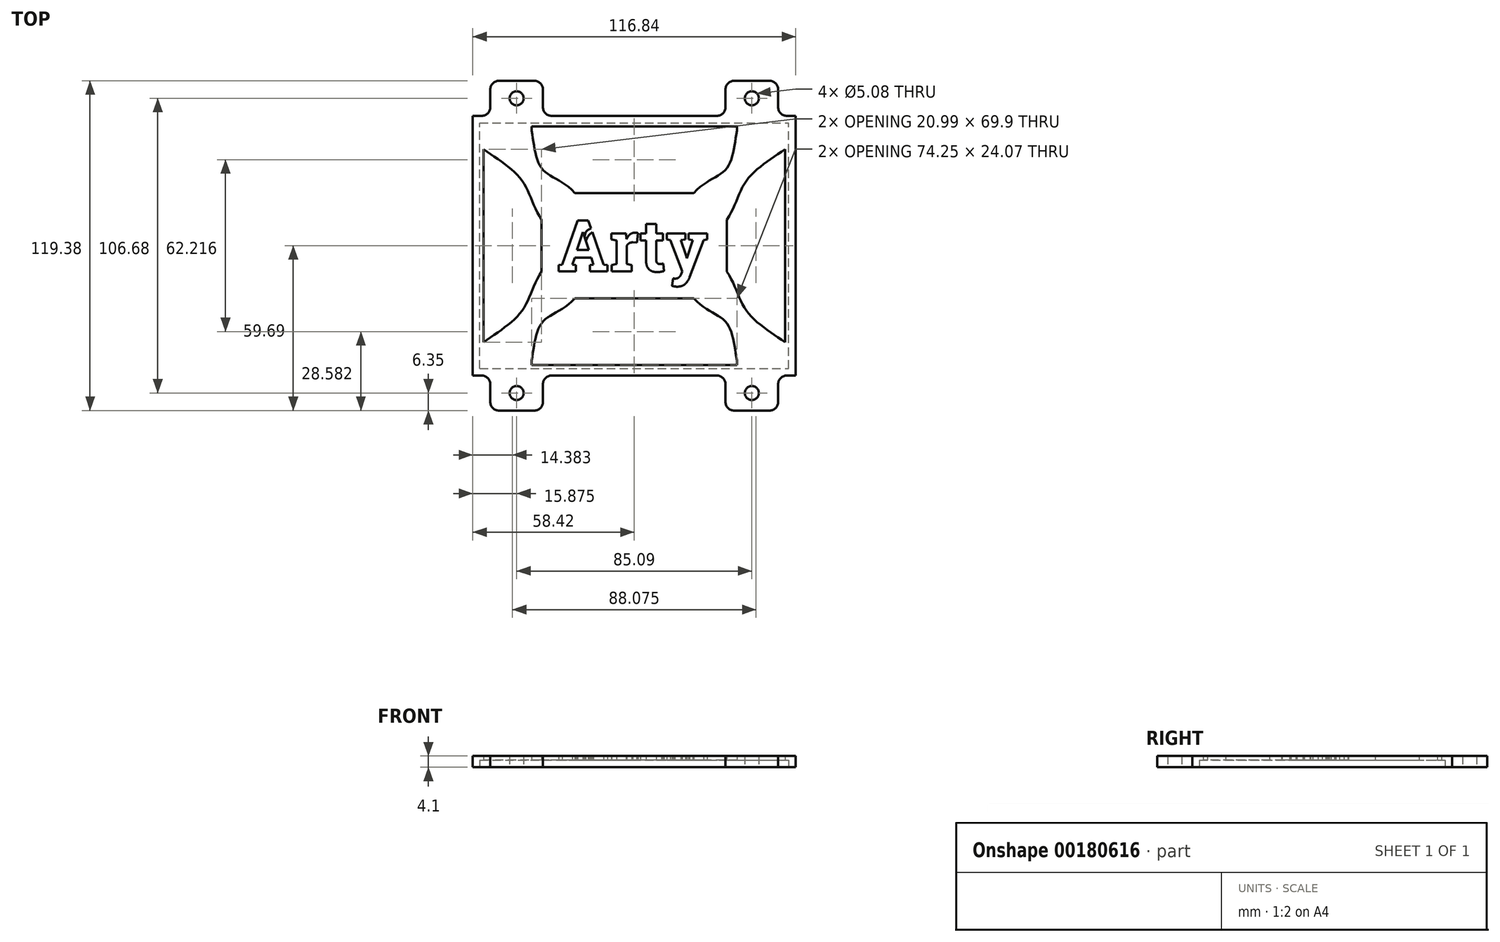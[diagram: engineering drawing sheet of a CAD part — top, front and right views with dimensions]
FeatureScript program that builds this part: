
annotation { "Feature Type Name" : "Feature", "Feature Type Description" : "" }
export const myFeature = defineFeature(function(context is Context, id is Id, definition is map)
    precondition{}
    {
        {
            var Q0;
            Q0=qCreatedBy(makeId("Top.planeOp"),FACE);
            var sketch = newSketch(context, id + "F0", { "sketchPlane" : qUnion([Q0])});
            skLineSegment(sketch, "E0.bottom", {"start": v(58.42, -46.99) * mm, "end": v(-58.42, -46.99) * mm});
            skLineSegment(sketch, "E0.top", {"start": v(58.42, 47) * mm, "end": v(-58.42, 46.99) * mm});
            skLineSegment(sketch, "E0.left", {"start": v(58.42, -46.99) * mm, "end": v(58.42, 47) * mm});
            skLineSegment(sketch, "E0.right", {"start": v(-58.42, -46.99) * mm, "end": v(-58.42, 46.99) * mm});
            skPoint(sketch, "E1", {"position": v(-58.42, 0) * mm});
            skPoint(sketch, "E2", {"position": v(0, 47) * mm});
            skSolve(sketch);
        }
        {
            var Q0;
            Q0 = qSketchRegion(id + "F0", true);
            extrude(context, id + "F1", {"entities" : qUnion([Q0]), "depth" : 4.1 * mm});
        }
        {
            var Q0;
            Q0=qCreatedBy(makeId("Top.planeOp"),FACE);
            var sketch = newSketch(context, id + "F2", { "sketchPlane" : qUnion([Q0])});
            skLineSegment(sketch, "E3.bottom", {"start": v(-55.88, -44.45) * mm, "end": v(55.88, -44.45) * mm});
            skLineSegment(sketch, "E3.top", {"start": v(-55.88, 44.45) * mm, "end": v(55.88, 44.45) * mm});
            skLineSegment(sketch, "E3.left", {"start": v(-55.88, -44.45) * mm, "end": v(-55.88, 44.45) * mm});
            skLineSegment(sketch, "E3.right", {"start": v(55.88, -44.45) * mm, "end": v(55.88, 44.45) * mm});
            skPoint(sketch, "E4", {"position": v(0, 44.45) * mm});
            skPoint(sketch, "E5", {"position": v(55.88, 0) * mm});
            skSolve(sketch);
        }
        {
            var Q0;
            Q0=makeQuery(id+"F2.imprint","IMPRINT",FACE,{"disambiguationData":[TD([[makeQuery(id+"F2.imprint","IMPRINT",EDGE,{"derivedFrom":sQuery(id+"F2.wireOp",EDGE,"E3.bottom")}),1.0]])]});
            extrude(context, id + "F3", {"entities" : qUnion([Q0]), "operationType" : NewBodyOperationType.REMOVE, "depth" : 2.54 * mm});
        }
        {
            var Q0;
            Q0=makeQuery(id+"F1.opExtrude","SWEPT_FACE",FACE,{"disambiguationData":[OSD([sQuery(id+"F0.wireOp",EDGE,"E0.top")])]});
            var sketch = newSketch(context, id + "F4", { "sketchPlane" : qUnion([Q0])});
            skLineSegment(sketch, "E6.bottom", {"start": v(52.07, 0) * mm, "end": v(33.02, 0) * mm});
            skLineSegment(sketch, "E6.top", {"start": v(52.07, 4.1) * mm, "end": v(33.02, 4.1) * mm});
            skLineSegment(sketch, "E6.left", {"start": v(52.07, 0) * mm, "end": v(52.07, 4.1) * mm});
            skLineSegment(sketch, "E6.right", {"start": v(33.02, 0) * mm, "end": v(33.02, 4.1) * mm});
            skPoint(sketch, "E7", {"position": v(58.42, 0) * mm});
            skPoint(sketch, "E8.MirrorP", {"position": v(-58.42, 0) * mm});
            skLineSegment(sketch, "E9.MirrorCS", {"start": v(-52.07, 0) * mm, "end": v(-52.07, 4.1) * mm});
            skLineSegment(sketch, "E10.MirrorCS", {"start": v(-52.07, 0) * mm, "end": v(-33.02, 0) * mm});
            skLineSegment(sketch, "E11.MirrorCS", {"start": v(-33.02, 0) * mm, "end": v(-33.02, 4.1) * mm});
            skLineSegment(sketch, "E12.MirrorCS", {"start": v(-52.07, 4.1) * mm, "end": v(-33.02, 4.1) * mm});
            skSolve(sketch);
        }
        {
            var Q0;
            Q0 = qSketchRegion(id + "F4", true);
            extrude(context, id + "F5", {"entities" : qUnion([Q0]), "operationType" : NewBodyOperationType.ADD, "depth" : 12.7 * mm});
        }
        {
            var Q0;
            Q0=makeQuery(id+"F1.opExtrude","SWEPT_FACE",FACE,{"disambiguationData":[OSD([sQuery(id+"F0.wireOp",EDGE,"E0.bottom")])]});
            var sketch = newSketch(context, id + "F6", { "sketchPlane" : qUnion([Q0])});
            skLineSegment(sketch, "E13.bottom", {"start": v(-52.07, 4.1) * mm, "end": v(-33.02, 4.1) * mm});
            skLineSegment(sketch, "E13.top", {"start": v(-52.07, 0) * mm, "end": v(-33.02, 0) * mm});
            skLineSegment(sketch, "E13.left", {"start": v(-52.07, 4.1) * mm, "end": v(-52.07, 0) * mm});
            skLineSegment(sketch, "E13.right", {"start": v(-33.02, 4.1) * mm, "end": v(-33.02, 0) * mm});
            skPoint(sketch, "E14", {"position": v(-58.42, 0) * mm});
            skLineSegment(sketch, "E15.MirrorCS", {"start": v(52.07, 0) * mm, "end": v(33.02, 0) * mm});
            skLineSegment(sketch, "E16.MirrorCS", {"start": v(33.02, 4.1) * mm, "end": v(33.02, 0) * mm});
            skLineSegment(sketch, "E17.MirrorCS", {"start": v(52.07, 4.1) * mm, "end": v(33.02, 4.1) * mm});
            skLineSegment(sketch, "E18.MirrorCS", {"start": v(52.07, 4.1) * mm, "end": v(52.07, 0) * mm});
            skPoint(sketch, "E19.MirrorP", {"position": v(58.42, 0) * mm});
            skSolve(sketch);
        }
        {
            var Q0;
            Q0 = qSketchRegion(id + "F6", true);
            extrude(context, id + "F7", {"entities" : qUnion([Q0]), "operationType" : NewBodyOperationType.ADD, "depth" : 12.7 * mm});
        }
        {
            var Q0;
            Q0=makeQuery(id+"F7.boolean.opBoolean","MERGE",FACE,{"derivedFrom":[makeQuery(id+"F5.boolean.opBoolean","MERGE",FACE,{"derivedFrom":[makeQuery(id+"F1.opExtrude","CAP_FACE",FACE,{"disambiguationData":[OSD([sQuery(id+"F0.wireOp",EDGE,"E0.bottom"),sQuery(id+"F0.wireOp",EDGE,"E0.top"),sQuery(id+"F0.wireOp",EDGE,"E0.left"),sQuery(id+"F0.wireOp",EDGE,"E0.right")])],"isStart":true}),makeQuery(id+"F5.opExtrude","SWEPT_FACE",FACE,{"disambiguationData":[OSD([sQuery(id+"F4.wireOp",EDGE,"E6.bottom")])]}),makeQuery(id+"F5.opExtrude","SWEPT_FACE",FACE,{"disambiguationData":[OSD([sQuery(id+"F4.wireOp",EDGE,"E10.MirrorCS")])]})]}),makeQuery(id+"F7.opExtrude","SWEPT_FACE",FACE,{"disambiguationData":[OSD([sQuery(id+"F6.wireOp",EDGE,"E13.top")])]}),makeQuery(id+"F7.opExtrude","SWEPT_FACE",FACE,{"disambiguationData":[OSD([sQuery(id+"F6.wireOp",EDGE,"E15.MirrorCS")])]})]});
            var sketch = newSketch(context, id + "F8", { "sketchPlane" : qUnion([Q0])});
            skPoint(sketch, "E20.visualSharp", {"position": v(52.07, 59.69) * mm});
            skArc(sketch, "E20.filletArc", {"start": v(52.07, 56.51) * mm, "mid": v(51.14, 58.76) * mm, "end": v(48.9, 59.69) * mm});
            skPoint(sketch, "E21.visualSharp", {"position": v(33.02, 59.69) * mm});
            skArc(sketch, "E21.filletArc", {"start": v(36.2, 59.69) * mm, "mid": v(33.95, 58.76) * mm, "end": v(33.02, 56.51) * mm});
            skArc(sketch, "E22.MirrorCS", {"start": v(-36.2, 59.69) * mm, "mid": v(-33.95, 58.76) * mm, "end": v(-33.02, 56.51) * mm});
            skPoint(sketch, "E23.MirrorP", {"position": v(-52.07, 59.69) * mm});
            skArc(sketch, "E24.MirrorCS", {"start": v(-52.07, 56.51) * mm, "mid": v(-51.14, 58.76) * mm, "end": v(-48.9, 59.69) * mm});
            skArc(sketch, "E25.MirrorCS", {"start": v(-52.07, -56.51) * mm, "mid": v(-51.14, -58.76) * mm, "end": v(-48.9, -59.69) * mm});
            skArc(sketch, "E26.MirrorCS", {"start": v(-36.2, -59.69) * mm, "mid": v(-33.95, -58.76) * mm, "end": v(-33.02, -56.51) * mm});
            skArc(sketch, "E27.MirrorCS", {"start": v(36.2, -59.69) * mm, "mid": v(33.95, -58.76) * mm, "end": v(33.02, -56.51) * mm});
            skArc(sketch, "E28.MirrorCS", {"start": v(52.07, -56.51) * mm, "mid": v(51.14, -58.76) * mm, "end": v(48.9, -59.69) * mm});
            skLineSegment(sketch, "E29", {"start": v(33.02, 59.69) * mm, "end": v(33.02, 56.51) * mm});
            skLineSegment(sketch, "E30", {"start": v(33.02, 59.69) * mm, "end": v(36.2, 59.69) * mm});
            skLineSegment(sketch, "E31", {"start": v(48.9, 59.69) * mm, "end": v(52.07, 59.69) * mm});
            skLineSegment(sketch, "E32", {"start": v(52.07, 56.51) * mm, "end": v(52.07, 59.69) * mm});
            skLineSegment(sketch, "E33.MirrorCS", {"start": v(-33.02, 59.69) * mm, "end": v(-33.02, 56.51) * mm});
            skLineSegment(sketch, "E34.MirrorCS", {"start": v(-33.02, 59.69) * mm, "end": v(-36.2, 59.69) * mm});
            skLineSegment(sketch, "E35.MirrorCS", {"start": v(-48.9, 59.69) * mm, "end": v(-52.07, 59.69) * mm});
            skLineSegment(sketch, "E36.MirrorCS", {"start": v(-52.07, 56.51) * mm, "end": v(-52.07, 59.69) * mm});
            skLineSegment(sketch, "E37.MirrorCS", {"start": v(-52.07, -56.51) * mm, "end": v(-52.07, -59.69) * mm});
            skLineSegment(sketch, "E38.MirrorCS", {"start": v(-48.9, -59.69) * mm, "end": v(-52.07, -59.69) * mm});
            skLineSegment(sketch, "E39.MirrorCS", {"start": v(-33.02, -59.69) * mm, "end": v(-36.2, -59.69) * mm});
            skLineSegment(sketch, "E40.MirrorCS", {"start": v(-33.02, -59.69) * mm, "end": v(-33.02, -56.51) * mm});
            skLineSegment(sketch, "E41.MirrorCS", {"start": v(52.07, -56.51) * mm, "end": v(52.07, -59.69) * mm});
            skLineSegment(sketch, "E42.MirrorCS", {"start": v(48.9, -59.69) * mm, "end": v(52.07, -59.69) * mm});
            skLineSegment(sketch, "E43.MirrorCS", {"start": v(33.02, -59.69) * mm, "end": v(33.02, -56.51) * mm});
            skLineSegment(sketch, "E44.MirrorCS", {"start": v(33.02, -59.69) * mm, "end": v(36.2, -59.69) * mm});
            skSolve(sketch);
        }
        {
            var Q0;
            Q0 = qSketchRegion(id + "F8", true);
            extrude(context, id + "F9", {"entities" : qUnion([Q0]), "operationType" : NewBodyOperationType.REMOVE, "oppositeDirection" : true, "depth" : 4.1 * mm});
        }
        {
            var Q0;
            Q0=makeQuery(id+"F7.boolean.opBoolean","MERGE",FACE,{"derivedFrom":[makeQuery(id+"F5.boolean.opBoolean","MERGE",FACE,{"derivedFrom":[makeQuery(id+"F1.opExtrude","CAP_FACE",FACE,{"disambiguationData":[OSD([sQuery(id+"F0.wireOp",EDGE,"E0.bottom"),sQuery(id+"F0.wireOp",EDGE,"E0.top"),sQuery(id+"F0.wireOp",EDGE,"E0.left"),sQuery(id+"F0.wireOp",EDGE,"E0.right")])],"isStart":true}),makeQuery(id+"F5.opExtrude","SWEPT_FACE",FACE,{"disambiguationData":[OSD([sQuery(id+"F4.wireOp",EDGE,"E6.bottom")])]}),makeQuery(id+"F5.opExtrude","SWEPT_FACE",FACE,{"disambiguationData":[OSD([sQuery(id+"F4.wireOp",EDGE,"E10.MirrorCS")])]})]}),makeQuery(id+"F7.opExtrude","SWEPT_FACE",FACE,{"disambiguationData":[OSD([sQuery(id+"F6.wireOp",EDGE,"E13.top")])]}),makeQuery(id+"F7.opExtrude","SWEPT_FACE",FACE,{"disambiguationData":[OSD([sQuery(id+"F6.wireOp",EDGE,"E15.MirrorCS")])]})]});
            var sketch = newSketch(context, id + "F10", { "sketchPlane" : qUnion([Q0])});
            skPoint(sketch, "E45.visualSharp", {"position": v(-52.07, -46.99) * mm});
            skArc(sketch, "E45.filletArc", {"start": v(-52.07, -50.16) * mm, "mid": v(-53, -47.92) * mm, "end": v(-55.25, -46.99) * mm});
            skPoint(sketch, "E46.visualSharp", {"position": v(-33.02, -46.99) * mm});
            skArc(sketch, "E46.filletArc", {"start": v(-29.84, -46.99) * mm, "mid": v(-32.1, -47.92) * mm, "end": v(-33.02, -50.16) * mm});
            skLineSegment(sketch, "E47", {"start": v(-52.07, -46.99) * mm, "end": v(-52.07, -50.16) * mm});
            skLineSegment(sketch, "E48", {"start": v(-55.25, -46.99) * mm, "end": v(-52.07, -46.99) * mm});
            skLineSegment(sketch, "E49", {"start": v(-33.02, -50.16) * mm, "end": v(-33.02, -46.99) * mm});
            skLineSegment(sketch, "E50.MirrorCS", {"start": v(55.25, -46.99) * mm, "end": v(52.07, -46.99) * mm});
            skLineSegment(sketch, "E51.MirrorCS", {"start": v(33.02, -50.16) * mm, "end": v(33.02, -46.99) * mm});
            skArc(sketch, "E52.MirrorCS", {"start": v(29.84, -46.99) * mm, "mid": v(32.1, -47.92) * mm, "end": v(33.02, -50.16) * mm});
            skArc(sketch, "E53.MirrorCS", {"start": v(52.07, -50.16) * mm, "mid": v(53, -47.92) * mm, "end": v(55.25, -46.99) * mm});
            skLineSegment(sketch, "E54.MirrorCS", {"start": v(52.07, -46.99) * mm, "end": v(52.07, -50.16) * mm});
            skPoint(sketch, "E55.MirrorP", {"position": v(52.07, -46.99) * mm});
            skPoint(sketch, "E56.MirrorP", {"position": v(33.02, -46.99) * mm});
            skLineSegment(sketch, "E57.MirrorCS", {"start": v(52.07, 46.99) * mm, "end": v(52.07, 50.16) * mm});
            skLineSegment(sketch, "E58.MirrorCS", {"start": v(-55.25, 46.99) * mm, "end": v(-52.07, 46.99) * mm});
            skLineSegment(sketch, "E59.MirrorCS", {"start": v(55.25, 46.99) * mm, "end": v(52.07, 46.99) * mm});
            skArc(sketch, "E60.MirrorCS", {"start": v(52.07, 50.16) * mm, "mid": v(53, 47.92) * mm, "end": v(55.25, 46.99) * mm});
            skLineSegment(sketch, "E61.MirrorCS", {"start": v(-33.02, 50.16) * mm, "end": v(-33.02, 46.99) * mm});
            skLineSegment(sketch, "E62.MirrorCS", {"start": v(-52.07, 46.99) * mm, "end": v(-52.07, 50.16) * mm});
            skArc(sketch, "E63.MirrorCS", {"start": v(-52.07, 50.16) * mm, "mid": v(-53, 47.92) * mm, "end": v(-55.25, 46.99) * mm});
            skArc(sketch, "E64.MirrorCS", {"start": v(-29.84, 46.99) * mm, "mid": v(-32.1, 47.92) * mm, "end": v(-33.02, 50.16) * mm});
            skArc(sketch, "E65.MirrorCS", {"start": v(29.84, 46.99) * mm, "mid": v(32.1, 47.92) * mm, "end": v(33.02, 50.16) * mm});
            skLineSegment(sketch, "E66.MirrorCS", {"start": v(33.02, 50.16) * mm, "end": v(33.02, 46.99) * mm});
            skPoint(sketch, "E67.MirrorP", {"position": v(-52.07, 46.99) * mm});
            skPoint(sketch, "E68.MirrorP", {"position": v(-33.02, 46.99) * mm});
            skPoint(sketch, "E69.MirrorP", {"position": v(33.02, 46.99) * mm});
            skPoint(sketch, "E70.MirrorP", {"position": v(52.07, 46.99) * mm});
            skLineSegment(sketch, "E71", {"start": v(-33.02, -46.99) * mm, "end": v(-29.84, -46.99) * mm});
            skLineSegment(sketch, "E72", {"start": v(33.02, -46.99) * mm, "end": v(29.84, -46.99) * mm});
            skLineSegment(sketch, "E73", {"start": v(33.02, 46.99) * mm, "end": v(29.84, 46.99) * mm});
            skLineSegment(sketch, "E74", {"start": v(-33.02, 46.99) * mm, "end": v(-29.84, 46.99) * mm});
            skSolve(sketch);
        }
        {
            var Q0;
            Q0 = qSketchRegion(id + "F10", true);
            extrude(context, id + "F11", {"entities" : qUnion([Q0]), "operationType" : NewBodyOperationType.ADD, "oppositeDirection" : true, "depth" : 4.1 * mm});
        }
        {
            var Q0;
            Q0=makeQuery(id+"F11.boolean.opBoolean","MERGE",FACE,{"derivedFrom":[makeQuery(id+"F7.boolean.opBoolean","MERGE",FACE,{"derivedFrom":[makeQuery(id+"F5.boolean.opBoolean","MERGE",FACE,{"derivedFrom":[makeQuery(id+"F1.opExtrude","CAP_FACE",FACE,{"disambiguationData":[OSD([sQuery(id+"F0.wireOp",EDGE,"E0.bottom"),sQuery(id+"F0.wireOp",EDGE,"E0.top"),sQuery(id+"F0.wireOp",EDGE,"E0.left"),sQuery(id+"F0.wireOp",EDGE,"E0.right")])],"isStart":true}),makeQuery(id+"F5.opExtrude","SWEPT_FACE",FACE,{"disambiguationData":[OSD([sQuery(id+"F4.wireOp",EDGE,"E6.bottom")])]}),makeQuery(id+"F5.opExtrude","SWEPT_FACE",FACE,{"disambiguationData":[OSD([sQuery(id+"F4.wireOp",EDGE,"E10.MirrorCS")])]})]}),makeQuery(id+"F7.opExtrude","SWEPT_FACE",FACE,{"disambiguationData":[OSD([sQuery(id+"F6.wireOp",EDGE,"E13.top")])]}),makeQuery(id+"F7.opExtrude","SWEPT_FACE",FACE,{"disambiguationData":[OSD([sQuery(id+"F6.wireOp",EDGE,"E15.MirrorCS")])]})]}),makeQuery(id+"F11.opExtrude","CAP_FACE",FACE,{"disambiguationData":[OSD([sQuery(id+"F10.wireOp",EDGE,"E45.filletArc"),sQuery(id+"F10.wireOp",EDGE,"E47"),sQuery(id+"F10.wireOp",EDGE,"E48")])],"isStart":true}),makeQuery(id+"F11.opExtrude","CAP_FACE",FACE,{"disambiguationData":[OSD([sQuery(id+"F10.wireOp",EDGE,"E46.filletArc"),sQuery(id+"F10.wireOp",EDGE,"E49"),sQuery(id+"F10.wireOp",EDGE,"E71")])],"isStart":true}),makeQuery(id+"F11.opExtrude","CAP_FACE",FACE,{"disambiguationData":[OSD([sQuery(id+"F10.wireOp",EDGE,"E50.MirrorCS"),sQuery(id+"F10.wireOp",EDGE,"E53.MirrorCS"),sQuery(id+"F10.wireOp",EDGE,"E54.MirrorCS")])],"isStart":true}),makeQuery(id+"F11.opExtrude","CAP_FACE",FACE,{"disambiguationData":[OSD([sQuery(id+"F10.wireOp",EDGE,"E51.MirrorCS"),sQuery(id+"F10.wireOp",EDGE,"E52.MirrorCS"),sQuery(id+"F10.wireOp",EDGE,"E72")])],"isStart":true}),makeQuery(id+"F11.opExtrude","CAP_FACE",FACE,{"disambiguationData":[OSD([sQuery(id+"F10.wireOp",EDGE,"E57.MirrorCS"),sQuery(id+"F10.wireOp",EDGE,"E59.MirrorCS"),sQuery(id+"F10.wireOp",EDGE,"E60.MirrorCS")])],"isStart":true}),makeQuery(id+"F11.opExtrude","CAP_FACE",FACE,{"disambiguationData":[OSD([sQuery(id+"F10.wireOp",EDGE,"E58.MirrorCS"),sQuery(id+"F10.wireOp",EDGE,"E62.MirrorCS"),sQuery(id+"F10.wireOp",EDGE,"E63.MirrorCS")])],"isStart":true}),makeQuery(id+"F11.opExtrude","CAP_FACE",FACE,{"disambiguationData":[OSD([sQuery(id+"F10.wireOp",EDGE,"E61.MirrorCS"),sQuery(id+"F10.wireOp",EDGE,"E64.MirrorCS"),sQuery(id+"F10.wireOp",EDGE,"E74")])],"isStart":true}),makeQuery(id+"F11.opExtrude","CAP_FACE",FACE,{"disambiguationData":[OSD([sQuery(id+"F10.wireOp",EDGE,"E65.MirrorCS"),sQuery(id+"F10.wireOp",EDGE,"E66.MirrorCS"),sQuery(id+"F10.wireOp",EDGE,"E73")])],"isStart":true})]});
            var sketch = newSketch(context, id + "F12", { "sketchPlane" : qUnion([Q0])});
            skCircle(sketch, "E75", {"center": v(42.54, 53.34) * mm, "radius": 2.54 * mm});
            skPoint(sketch, "E75.centerSnap0", {"position": v(42.54, 59.69) * mm});
            skPoint(sketch, "E76.MirrorP", {"position": v(-42.54, 59.69) * mm});
            skCircle(sketch, "E77.MirrorC", {"center": v(-42.54, 53.34) * mm, "radius": 2.54 * mm});
            skPoint(sketch, "E78.MirrorP", {"position": v(42.54, -59.69) * mm});
            skCircle(sketch, "E79.MirrorC", {"center": v(-42.54, -53.34) * mm, "radius": 2.54 * mm});
            skCircle(sketch, "E80.MirrorC", {"center": v(42.54, -53.34) * mm, "radius": 2.54 * mm});
            skPoint(sketch, "E81.MirrorP", {"position": v(-42.54, -59.69) * mm});
            skSolve(sketch);
        }
        {
            var Q0;
            Q0=makeQuery(id+"F2.imprint","IMPRINT",FACE,{"disambiguationData":[TD([[makeQuery(id+"F2.imprint","IMPRINT",EDGE,{"derivedFrom":sQuery(id+"F2.wireOp",EDGE,"E3.bottom")}),1.0]])]});
            var sketch = newSketch(context, id + "F13", { "sketchPlane" : qUnion([Q0])});
            skText(sketch, "E82", { "text": "Arty", "fontName": "RobotoSlab-Bold.ttf"});
            skFitSpline(sketch, "E83", {"points": [v(33.54, 9.43) * mm, v(40.7, 23.68) * mm, v(54.53, 34.95) * mm], "startDerivative": vector(19.96, 30) * mm, "endDerivative": vector(29.2, 21.05) * mm});
            skFitSpline(sketch, "E84", {"points": [v(21.5, 19.07) * mm, v(33.28, 27.78) * mm, v(37.12, 41.6) * mm], "startDerivative": vector(26, 29.14) * mm, "endDerivative": vector(5.18, 30.3) * mm});
            skLineSegment(sketch, "E85", {"start": v(21.5, 19.07) * mm, "end": v(0, 19.07) * mm});
            skLineSegment(sketch, "E86", {"start": v(0, 43.14) * mm, "end": v(37.12, 43.14) * mm});
            skLineSegment(sketch, "E87", {"start": v(37.12, 43.14) * mm, "end": v(37.12, 41.6) * mm});
            skLineSegment(sketch, "E88", {"start": v(54.53, 34.95) * mm, "end": v(54.53, 0) * mm});
            skLineSegment(sketch, "E89", {"start": v(33.54, 9.43) * mm, "end": v(33.54, 0) * mm});
            skLineSegment(sketch, "E90.MirrorCS", {"start": v(-37.12, 43.14) * mm, "end": v(-37.12, 41.6) * mm});
            skFitSpline(sketch, "E91.MirrorCS", {"points": [v(-33.54, 9.43) * mm, v(-40.7, 23.68) * mm, v(-54.53, 34.95) * mm], "startDerivative": vector(-19.96, 30) * mm, "endDerivative": vector(-29.2, 21.05) * mm});
            skLineSegment(sketch, "E92.MirrorCS", {"start": v(0, 43.14) * mm, "end": v(-37.12, 43.14) * mm});
            skLineSegment(sketch, "E93.MirrorCS", {"start": v(-33.54, 9.43) * mm, "end": v(-33.54, 0) * mm});
            skLineSegment(sketch, "E94.MirrorCS", {"start": v(-54.53, 34.95) * mm, "end": v(-54.53, 0) * mm});
            skLineSegment(sketch, "E95.MirrorCS", {"start": v(-21.5, 19.07) * mm, "end": v(0, 19.07) * mm});
            skFitSpline(sketch, "E96.MirrorCS", {"points": [v(-21.5, 19.07) * mm, v(-33.28, 27.78) * mm, v(-37.12, 41.6) * mm], "startDerivative": vector(-26, 29.14) * mm, "endDerivative": vector(-5.18, 30.3) * mm});
            skLineSegment(sketch, "E97.MirrorCS", {"start": v(-37.12, -43.14) * mm, "end": v(-37.12, -41.6) * mm});
            skLineSegment(sketch, "E98.MirrorCS", {"start": v(37.12, -43.14) * mm, "end": v(37.12, -41.6) * mm});
            skLineSegment(sketch, "E99.MirrorCS", {"start": v(0, -43.14) * mm, "end": v(-37.12, -43.14) * mm});
            skFitSpline(sketch, "E100.MirrorCS", {"points": [v(-33.54, -9.43) * mm, v(-40.7, -23.68) * mm, v(-54.53, -34.95) * mm], "startDerivative": vector(-19.96, -30) * mm, "endDerivative": vector(-29.2, -21.05) * mm});
            skFitSpline(sketch, "E101.MirrorCS", {"points": [v(33.54, -9.43) * mm, v(40.7, -23.68) * mm, v(54.53, -34.95) * mm], "startDerivative": vector(19.96, -30) * mm, "endDerivative": vector(29.2, -21.05) * mm});
            skFitSpline(sketch, "E102.MirrorCS", {"points": [v(21.5, -19.07) * mm, v(33.28, -27.78) * mm, v(37.12, -41.6) * mm], "startDerivative": vector(26, -29.14) * mm, "endDerivative": vector(5.18, -30.3) * mm});
            skLineSegment(sketch, "E103.MirrorCS", {"start": v(-54.53, -34.95) * mm, "end": v(-54.53, 0) * mm});
            skLineSegment(sketch, "E104.MirrorCS", {"start": v(21.5, -19.07) * mm, "end": v(0, -19.07) * mm});
            skLineSegment(sketch, "E105.MirrorCS", {"start": v(-21.5, -19.07) * mm, "end": v(0, -19.07) * mm});
            skLineSegment(sketch, "E106.MirrorCS", {"start": v(54.53, -34.95) * mm, "end": v(54.53, 0) * mm});
            skFitSpline(sketch, "E107.MirrorCS", {"points": [v(-21.5, -19.07) * mm, v(-33.28, -27.78) * mm, v(-37.12, -41.6) * mm], "startDerivative": vector(-26, -29.14) * mm, "endDerivative": vector(-5.18, -30.3) * mm});
            skLineSegment(sketch, "E108.MirrorCS", {"start": v(33.54, -9.43) * mm, "end": v(33.54, 0) * mm});
            skLineSegment(sketch, "E109.MirrorCS", {"start": v(0, -43.14) * mm, "end": v(37.12, -43.14) * mm});
            skLineSegment(sketch, "E110.MirrorCS", {"start": v(-33.54, -9.43) * mm, "end": v(-33.54, 0) * mm});
            const initialGuessF13  = {"E82": [-0.0279, -0.00929, 1, 0, 0.01871]};
            skSetInitialGuess(sketch, initialGuessF13);
            skSolve(sketch);
        }
        {
            var Q0;
            Q0 = qSketchRegion(id + "F13", true);
            extrude(context, id + "F14", {"entities" : qUnion([Q0]), "operationType" : NewBodyOperationType.REMOVE, "depth" : 25.4 * mm});
        }
        {
            var Q0;
            Q0 = qSketchRegion(id + "F12", true);
            extrude(context, id + "F15", {"entities" : qUnion([Q0]), "operationType" : NewBodyOperationType.REMOVE, "oppositeDirection" : true, "depth" : 5.08 * mm});
        }
        {
            var Q0;
            Q0=makeQuery(id+"F14.boolean.opBoolean","SPLIT",FACE,{"disambiguationData":[TD([makeQuery(id+"F14.opExtrude","SWEPT_FACE",FACE,{"disambiguationData":[OSD([sQuery(id+"F13.wireOp",EDGE,"E82.sketch_text.stroke-16")])]})])],"derivedFrom":makeQuery(id+"F11.boolean.opBoolean","MERGE",FACE,{"derivedFrom":[makeQuery(id+"F7.boolean.opBoolean","MERGE",FACE,{"derivedFrom":[makeQuery(id+"F5.boolean.opBoolean","MERGE",FACE,{"derivedFrom":[makeQuery(id+"F1.opExtrude","CAP_FACE",FACE,{"disambiguationData":[OSD([sQuery(id+"F0.wireOp",EDGE,"E0.bottom"),sQuery(id+"F0.wireOp",EDGE,"E0.top"),sQuery(id+"F0.wireOp",EDGE,"E0.left"),sQuery(id+"F0.wireOp",EDGE,"E0.right")])],"isStart":false}),makeQuery(id+"F5.opExtrude","SWEPT_FACE",FACE,{"disambiguationData":[OSD([sQuery(id+"F4.wireOp",EDGE,"E6.top")])]}),makeQuery(id+"F5.opExtrude","SWEPT_FACE",FACE,{"disambiguationData":[OSD([sQuery(id+"F4.wireOp",EDGE,"E12.MirrorCS")])]})]}),makeQuery(id+"F7.opExtrude","SWEPT_FACE",FACE,{"disambiguationData":[OSD([sQuery(id+"F6.wireOp",EDGE,"E13.bottom")])]}),makeQuery(id+"F7.opExtrude","SWEPT_FACE",FACE,{"disambiguationData":[OSD([sQuery(id+"F6.wireOp",EDGE,"E17.MirrorCS")])]})]}),makeQuery(id+"F11.opExtrude","CAP_FACE",FACE,{"disambiguationData":[OSD([sQuery(id+"F10.wireOp",EDGE,"E45.filletArc"),sQuery(id+"F10.wireOp",EDGE,"E47"),sQuery(id+"F10.wireOp",EDGE,"E48")])],"isStart":false}),makeQuery(id+"F11.opExtrude","CAP_FACE",FACE,{"disambiguationData":[OSD([sQuery(id+"F10.wireOp",EDGE,"E46.filletArc"),sQuery(id+"F10.wireOp",EDGE,"E49"),sQuery(id+"F10.wireOp",EDGE,"E71")])],"isStart":false}),makeQuery(id+"F11.opExtrude","CAP_FACE",FACE,{"disambiguationData":[OSD([sQuery(id+"F10.wireOp",EDGE,"E50.MirrorCS"),sQuery(id+"F10.wireOp",EDGE,"E53.MirrorCS"),sQuery(id+"F10.wireOp",EDGE,"E54.MirrorCS")])],"isStart":false}),makeQuery(id+"F11.opExtrude","CAP_FACE",FACE,{"disambiguationData":[OSD([sQuery(id+"F10.wireOp",EDGE,"E51.MirrorCS"),sQuery(id+"F10.wireOp",EDGE,"E52.MirrorCS"),sQuery(id+"F10.wireOp",EDGE,"E72")])],"isStart":false}),makeQuery(id+"F11.opExtrude","CAP_FACE",FACE,{"disambiguationData":[OSD([sQuery(id+"F10.wireOp",EDGE,"E57.MirrorCS"),sQuery(id+"F10.wireOp",EDGE,"E59.MirrorCS"),sQuery(id+"F10.wireOp",EDGE,"E60.MirrorCS")])],"isStart":false}),makeQuery(id+"F11.opExtrude","CAP_FACE",FACE,{"disambiguationData":[OSD([sQuery(id+"F10.wireOp",EDGE,"E58.MirrorCS"),sQuery(id+"F10.wireOp",EDGE,"E62.MirrorCS"),sQuery(id+"F10.wireOp",EDGE,"E63.MirrorCS")])],"isStart":false}),makeQuery(id+"F11.opExtrude","CAP_FACE",FACE,{"disambiguationData":[OSD([sQuery(id+"F10.wireOp",EDGE,"E61.MirrorCS"),sQuery(id+"F10.wireOp",EDGE,"E64.MirrorCS"),sQuery(id+"F10.wireOp",EDGE,"E74")])],"isStart":false}),makeQuery(id+"F11.opExtrude","CAP_FACE",FACE,{"disambiguationData":[OSD([sQuery(id+"F10.wireOp",EDGE,"E65.MirrorCS"),sQuery(id+"F10.wireOp",EDGE,"E66.MirrorCS"),sQuery(id+"F10.wireOp",EDGE,"E73")])],"isStart":false})]})});
            var sketch = newSketch(context, id + "F16", { "sketchPlane" : qUnion([Q0])});
            skFitSpline(sketch, "E111", {"points": [v(-17.98, 3.24) * mm, v(-17.3, 5.15) * mm, v(-15.38, 6.44) * mm], "startDerivative": vector(0.84, 4.3) * mm, "endDerivative": vector(4.31, 2.12) * mm});
            skFitSpline(sketch, "E112", {"points": [v(-17.48, 1.68) * mm, v(-16.44, 3.74) * mm, v(-15.06, 4.94) * mm], "startDerivative": vector(1.72, 4.23) * mm, "endDerivative": vector(3.15, 2.24) * mm});
            skLineSegment(sketch, "E113", {"start": v(-15.06, 4.94) * mm, "end": v(-15.38, 6.44) * mm});
            skLineSegment(sketch, "E114", {"start": v(-17.48, 1.68) * mm, "end": v(-17.98, 3.24) * mm});
            skSolve(sketch);
        }
        {
            var Q0;
            Q0 = qSketchRegion(id + "F16", true);
            extrude(context, id + "F17", {"entities" : qUnion([Q0]), "operationType" : NewBodyOperationType.ADD, "oppositeDirection" : true, "depth" : 1.56 * mm});
        }
    });
